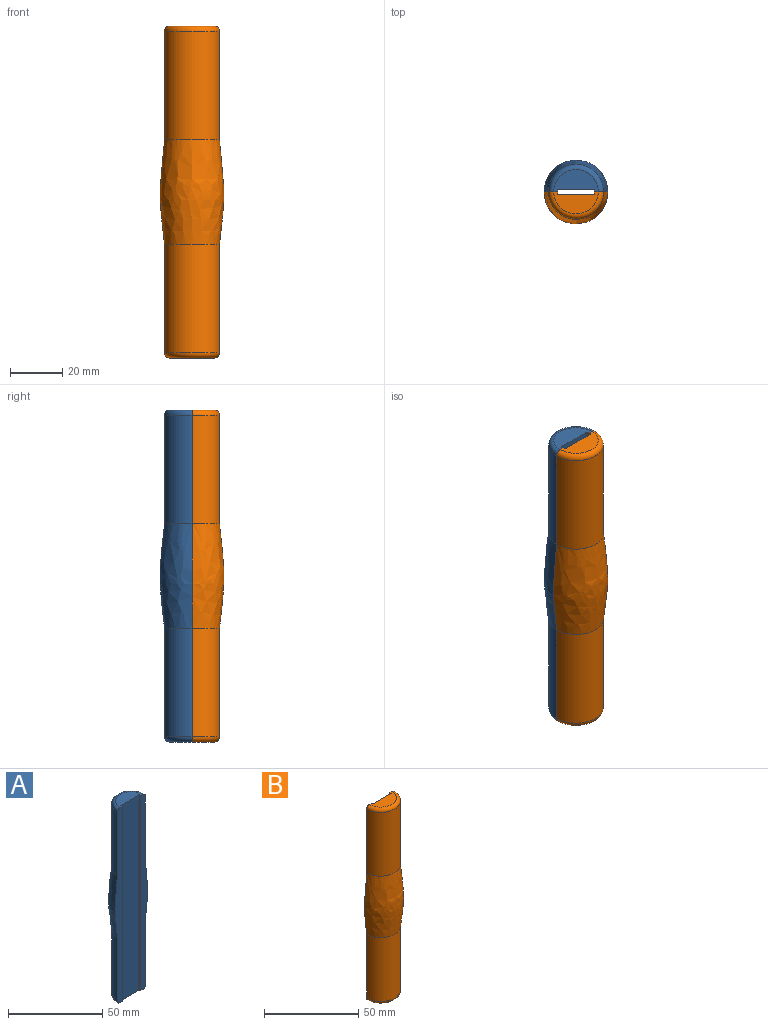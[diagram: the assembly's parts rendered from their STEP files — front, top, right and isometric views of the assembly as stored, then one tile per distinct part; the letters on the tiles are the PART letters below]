
ASSEMBLY  parts=2 mates=1
PART A: 14 faces, bbox 24.6x12.2x127 mm
  f0: plane 127x5.28mm, normal (0,-1,0), area 483.8mm2, adj f1,f2,f3,f4,f5,f9,f12,f13
  f1: plane 17x8.5mm, normal (0,0,-1), area 99.5mm2, adj f0,f6,f7,f8,f9,f10,f11,f13
  f2: plane 17x8.5mm, normal (0,0,1), area 99.5mm2, adj f0,f6,f7,f8,f9,f10,f11,f12
  f3: cylinder r=10.5mm len=41.5mm, axis (0,0,1), area 1368.9mm2, adj f0,f5,f6,f13
  f4: cylinder r=10.5mm len=41.5mm, axis (0,0,1), area 1368.9mm2, adj f0,f5,f6,f12
  f5: revolved ~40x24.42mm, area 1454.1mm2, adj f0,f3,f4,f6
  f6: plane 127x5.28mm, normal (0,-1,0), area 483.8mm2, adj f1,f2,f3,f4,f5,f8,f12,f13
  f7: cylinder r=0.3mm len=127mm, axis (0,0,1), area 59.8mm2, adj f1,f2,f8,f11
  f8: plane 127x0.7mm, normal (1,0,0), area 88.9mm2, adj f1,f2,f6,f7
  f9: plane 127x0.7mm, normal (-1,0,0), area 88.9mm2, adj f0,f1,f2,f10
  f10: cylinder r=0.3mm len=127mm, axis (0,0,1), area 59.8mm2, adj f1,f2,f9,f11
  f11: plane 127x13.4mm, normal (0,-1,0), area 1701.8mm2, adj f1,f2,f7,f10
  f12: torus R=8.5mm, axis (0,0,-1), area 96.5mm2, adj f0,f2,f4,f6
  f13: torus R=8.5mm, axis (0,0,-1), area 96.5mm2, adj f0,f1,f3,f6
PART B: 14 faces, bbox 24.6x12.2x127 mm
  f0: plane 127x5.28mm, normal (0,1,0), area 483.8mm2, adj f1,f2,f3,f4,f5,f9,f12,f13
  f1: plane 17x8.5mm, normal (0,0,-1), area 99.5mm2, adj f0,f6,f7,f8,f9,f10,f11,f13
  f2: plane 17x8.5mm, normal (0,0,1), area 99.5mm2, adj f0,f6,f7,f8,f9,f10,f11,f12
  f3: cylinder r=10.5mm len=41.5mm, axis (0,0,1), area 1368.9mm2, adj f0,f5,f6,f13
  f4: cylinder r=10.5mm len=41.5mm, axis (0,0,1), area 1368.9mm2, adj f0,f5,f6,f12
  f5: revolved ~40x24.42mm, area 1454.1mm2, adj f0,f3,f4,f6
  f6: plane 127x5.28mm, normal (0,1,0), area 483.8mm2, adj f1,f2,f3,f4,f5,f8,f12,f13
  f7: cylinder r=0.3mm len=127mm, axis (0,0,1), area 59.8mm2, adj f1,f2,f8,f11
  f8: plane 127x0.7mm, normal (1,0,0), area 88.9mm2, adj f1,f2,f6,f7
  f9: plane 127x0.7mm, normal (-1,0,0), area 88.9mm2, adj f0,f1,f2,f10
  f10: cylinder r=0.3mm len=127mm, axis (0,0,1), area 59.8mm2, adj f1,f2,f9,f11
  f11: plane 127x13.4mm, normal (0,1,0), area 1701.8mm2, adj f1,f2,f7,f10
  f12: torus R=8.5mm, axis (0,0,-1), area 96.5mm2, adj f0,f2,f4,f6
  f13: torus R=8.5mm, axis (0,0,-1), area 96.5mm2, adj f0,f1,f3,f6
PLACE A t=(-27.63,-5.94,1.12)mm
PLACE B t=(-27.63,-5.94,1.12)mm
MATE fastened A.f0 <-> B.f0  axis (0,-1,0) through (-13.43,-5.94,1.1)mm
